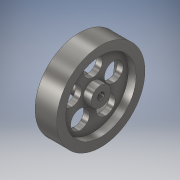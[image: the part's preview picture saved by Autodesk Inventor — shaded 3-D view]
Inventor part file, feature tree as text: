
AUTODESK INVENTOR PART (.ipt)
format: ipt  version: 2018 (Build 220112000, 112)  size: 160,768 bytes
history: native  units: in
note: dims shown in document units (in); Inventor stores cm internally (conversion verified against a paired STEP export)
features: sketch x2, revolve x1, thread x1, extrude x1
ambient origin geometry x8: Origin, YZ Plane, XZ Plane, XY Plane, X Axis, Y Axis, Z Axis, Center Point
bodies: Body1 (feature_tree)
feature tree (5):
  revolve  "Revolution1"  [1 undecoded]
  thread  "Thread1"  [1 undecoded]
  extrude  "Extrusion3"  Depth=0.1in
  sketch  "Sketch3"  dims[d10=0.045in d11=0.274in d12=0.077in]
  sketch  "Sketch4"  dims[d13=0.1in d14=0.1in d15=0.323in d16=0.112in d17=90.0deg d18=1.0in d19=0.0in d20=0.239in d21=1.9685in d23=360.0deg d25=0.275in d26=0.0in]
note: 2 required parameter values undecoded (feature->parameter linkage not recoverable at this tier; creation-order binding heuristic only, values carry confidence <= 0.55)